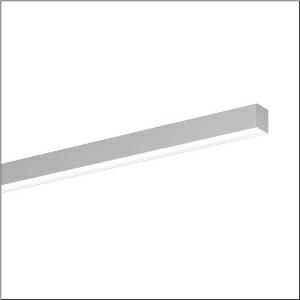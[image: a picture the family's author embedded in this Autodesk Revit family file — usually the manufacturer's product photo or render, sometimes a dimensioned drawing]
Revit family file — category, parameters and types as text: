
# Revit family: silica_r__21_51mx20tbt2s_686e
name_source: partatom
category: Lighting Fixtures
units: mm (PartAtom-declared; Revit-internal decimal feet)

## family parameters
Cut with Voids When Loaded = No
Host = Face
Light Source = No
Part Type = Normal
Room Calculation Point = No
Round Connector Dimension = Use Diameter
Shared = No

## types (1)
- --- (1 x LED, 3000 lm, 25.6 W, 6500K)
    Apparent Load = 26 VA
    CIE Flux Codes = 48 79 96 100 100
    Color Rendering = 80
    Color Temperature = 6500K
    Default Elevation = 1800 mm
    Description = Silica® 21, office luminaire, primary optical cover: cover, of PMMA, opal, light emission: direct distribution, primary light characteristic: symmetric, installation type: surface-mounted, LED, rated luminous flux: 3.000lm, luminous efficacy: 112lm/W, light colour: 8tw, colour temperature: 2700..6500K, control gear: DALI DT8, with terminal, 3+2-pole, max. 2.5mm², mains connection: 220..240V, AC, 50/60Hz, rated input power: 26.9W, luminaire housing, of aluminium, metallic grey (RAL 9006), length: 1.504mm, width: 53mm, height: 53mm, protection rating (complete): IP20, insulation class (complete): insulation class I (protective earthing), certification: CE, permissible operating ambient temperature: 0..+35°C, standard: EN 50419, packaging unit: 1 piece
    Height = 53 mm
    Lamp = 1 x LED
    Lamp Light Flux = 3000 lm
    Lamp Power = 25.6 W
    Lamp count = 1
    Length = 1504 mm
    Luminous efficacy = 117 lm/W
    Manufacturer = Siteco
    ModVariant = No
    Model = 51MX20TBT2S
    Mounting Place = Ceiling
    Mounting Type = Surface mounted
    Number of Poles = 1
    OnlyDefault = Yes
    Power Factor = 1
    Product Name = Silica® 21
    Product group = office luminaire | ceiling mounted
    ProductGroupID = 302
    Protection Class = Protection class I
    Protection Degree = IP 20
    RLX_Detail_Level = 1
    RLX_Emergency_Light_Flux = 0 lm
    RLX_Emergency_Type = 0
    RLX_Emergency_Type_DB = No
    RlxData = <blob elided: 23225 chars, md5=6da57648>
    Socket = socket
    Standby Power = 0 W
    System Light Flux = 3000 lm
    System Power = 26 W
    Type Comments = individual setting
    Type Image = l_1335933.jpg
    URL = http://relux.com
    VarID = @adj_139668
    Voltage = 0 V
    Weight = 0.00 kg
    Width = 53 mm

## geometry (parser evidence)
native form markers: Blend x4, Sweep x11
no freeform markers — native parametric forms only
